# Revit family: Plumbing-Water-Closet-Combos-Sloan-Valve-WETS-24501404_
name_source: partatom
category: Plumbing Fixtures
units: mm (PartAtom-declared; Revit-internal decimal feet)

## family parameters
Cut with Voids When Loaded = No
Host = Face
OmniClass Number = 23.45.05.21.11.11
OmniClass Title = Water Operated Water Closets
Part Type = Normal
Room Calculation Point = No
Round Connector Dimension = Use Diameter
Shared = No

## types (1)
- WETS-2450.1404
    Assembly Code = D2010
    CW Connection = Yes
    CWFU = 0
    Default Elevation = 0"
    Depth = 26 3/4"
    Description = ST-2459 Water Closet and GEM-2 111 SFSM Flushometer.
    Edition number = 1
    Flush Rate = 1.28 gpf (4.8 Lpf)
    Flushometer Code = 3070065
    Flushometer Material = Sloan Valve - Finish - Polished Chrome
    HW Connection = No
    HWFU = 0
    Height = 13 1/4"
    Keynote = 15410
    Manufacturer = Sloan Valve
    Model = WETS-2450.1404
    Part Number = 24501404
    Product Material = Sloan Valve - Vitreous China - White
    Product data url = https://bimobject.com
    Sanitary Drain Connection Diameter = 2"
    URL = www.sloanvalve.com
    Valve Pressure Drop = 0.00 psi
    Vent Connection = No
    WFU = 10
    Waste Connection = Yes
    Water Closet Code = 2102459
    Water Inlet Connection Diameter = 1"
    Width = 15"

## geometry (parser evidence)
native form markers: Sweep x2
no freeform markers — native parametric forms only
